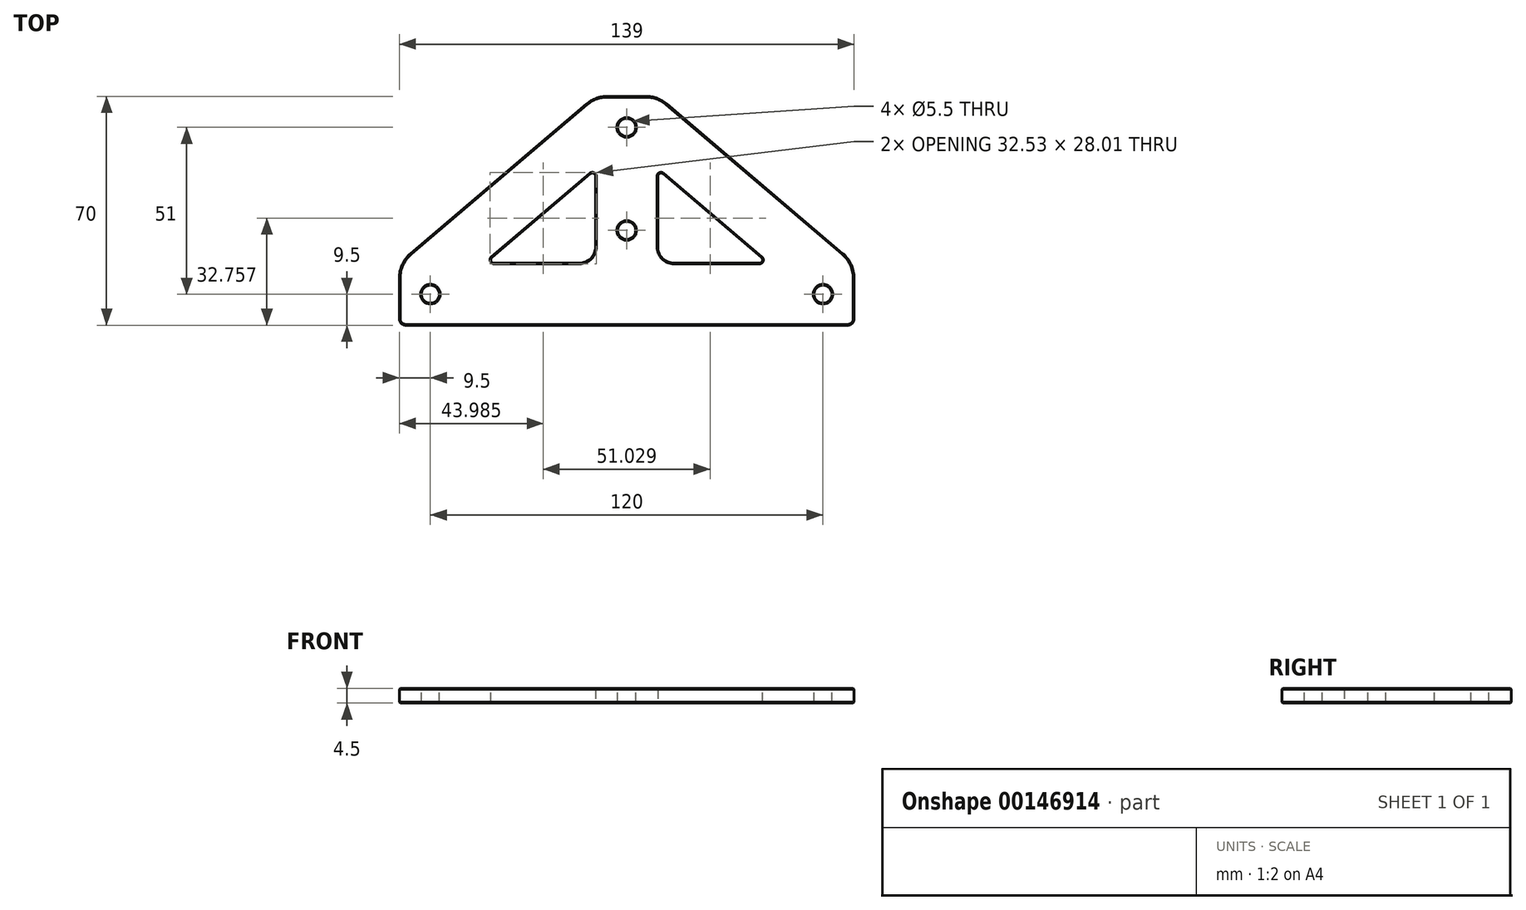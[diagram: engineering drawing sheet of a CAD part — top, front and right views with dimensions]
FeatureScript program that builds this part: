
annotation { "Feature Type Name" : "Feature", "Feature Type Description" : "" }
export const myFeature = defineFeature(function(context is Context, id is Id, definition is map)
    precondition{}
    {
        {
            var Q0;
            Q0=qCreatedBy(makeId("Top.planeOp"),FACE);
            var sketch = newSketch(context, id + "F0", { "sketchPlane" : qUnion([Q0])});
            skLineSegment(sketch, "E0", {"start": v(-69.5, 19) * mm, "end": v(-69.5, 0) * mm});
            skLineSegment(sketch, "E1", {"start": v(-69.5, 0) * mm, "end": v(69.5, 0) * mm});
            skLineSegment(sketch, "E2", {"start": v(69.5, 0) * mm, "end": v(69.5, 19) * mm});
            skLineSegment(sketch, "E3", {"start": v(69.5, 19) * mm, "end": v(9.5, 70) * mm});
            skLineSegment(sketch, "E4", {"start": v(9.5, 70) * mm, "end": v(-9.5, 70) * mm});
            skLineSegment(sketch, "E5", {"start": v(-9.5, 70) * mm, "end": v(-69.5, 19) * mm});
            skLineSegment(sketch, "E6", {"start": v(-9.5, 47.69) * mm, "end": v(-9.5, 19) * mm});
            skLineSegment(sketch, "E7", {"start": v(-9.5, 19) * mm, "end": v(-43.25, 19) * mm});
            skLineSegment(sketch, "E8", {"start": v(-43.25, 19) * mm, "end": v(-9.5, 47.69) * mm});
            skLineSegment(sketch, "E9.MirrorCS", {"start": v(9.5, 47.69) * mm, "end": v(9.5, 19) * mm});
            skLineSegment(sketch, "E10.MirrorCS", {"start": v(43.25, 19) * mm, "end": v(9.5, 47.69) * mm});
            skLineSegment(sketch, "E11.MirrorCS", {"start": v(9.5, 19) * mm, "end": v(43.25, 19) * mm});
            skSolve(sketch);
        }
        {
            var Q0;
            Q0 = qSketchRegion(id + "F0", true);
            extrude(context, id + "F1", {"entities" : qUnion([Q0]), "depth" : 4.5 * mm});
        }
        {
            var Q0;
            Q0=makeQuery(id+"F1.opExtrude","CAP_FACE",FACE,{"disambiguationData":[OSD([sQuery(id+"F0.wireOp",EDGE,"E0"),sQuery(id+"F0.wireOp",EDGE,"E1"),sQuery(id+"F0.wireOp",EDGE,"E2"),sQuery(id+"F0.wireOp",EDGE,"E3"),sQuery(id+"F0.wireOp",EDGE,"E4"),sQuery(id+"F0.wireOp",EDGE,"E5"),sQuery(id+"F0.wireOp",EDGE,"E6"),sQuery(id+"F0.wireOp",EDGE,"E7"),sQuery(id+"F0.wireOp",EDGE,"E8"),sQuery(id+"F0.wireOp",EDGE,"E9.MirrorCS"),sQuery(id+"F0.wireOp",EDGE,"E10.MirrorCS"),sQuery(id+"F0.wireOp",EDGE,"E11.MirrorCS")])],"isStart":false});
            var sketch = newSketch(context, id + "F2", { "sketchPlane" : qUnion([Q0])});
            skCircle(sketch, "E12", {"center": v(0, 60.5) * mm, "radius": 2.75 * mm});
            skCircle(sketch, "E13", {"center": v(0, 29) * mm, "radius": 2.75 * mm});
            skCircle(sketch, "E14", {"center": v(60, 9.5) * mm, "radius": 2.75 * mm});
            skCircle(sketch, "E15", {"center": v(-60, 9.5) * mm, "radius": 2.75 * mm});
            skSolve(sketch);
        }
        {
            var Q0;
            Q0 = qSketchRegion(id + "F2", true);
            extrude(context, id + "F3", {"entities" : qUnion([Q0]), "operationType" : NewBodyOperationType.REMOVE, "endBound" : BoundingType.THROUGH_ALL, "oppositeDirection" : true, "depth" : 25 * mm});
        }
        {
            var Q0;
            Q0=makeQuery(id+"F1.opExtrude","SWEPT_EDGE",EDGE,{"disambiguationData":[OSD([sQuery(id+"F0.wireOp",EDGE,"E6"),sQuery(id+"F0.wireOp",EDGE,"E7")])]});
            var Q1;
            Q1=makeQuery(id+"F1.opExtrude","SWEPT_EDGE",EDGE,{"disambiguationData":[OSD([sQuery(id+"F0.wireOp",EDGE,"E9.MirrorCS"),sQuery(id+"F0.wireOp",EDGE,"E11.MirrorCS")])]});
            fillet(context, id + "F4", {"entities" : qUnion([Q0, Q1]), "radius" : 5 * mm, "tangentPropagation" : true, "allowEdgeOverflow" : false});
        }
        {
            var Q0;
            Q0=makeQuery(id+"F1.opExtrude","SWEPT_EDGE",EDGE,{"disambiguationData":[OSD([sQuery(id+"F0.wireOp",EDGE,"E10.MirrorCS"),sQuery(id+"F0.wireOp",EDGE,"E11.MirrorCS")])]});
            var Q1;
            Q1=makeQuery(id+"F1.opExtrude","SWEPT_EDGE",EDGE,{"disambiguationData":[OSD([sQuery(id+"F0.wireOp",EDGE,"E9.MirrorCS"),sQuery(id+"F0.wireOp",EDGE,"E10.MirrorCS")])]});
            var Q2;
            Q2=makeQuery(id+"F1.opExtrude","SWEPT_EDGE",EDGE,{"disambiguationData":[OSD([sQuery(id+"F0.wireOp",EDGE,"E6"),sQuery(id+"F0.wireOp",EDGE,"E8")])]});
            var Q3;
            Q3=makeQuery(id+"F1.opExtrude","SWEPT_EDGE",EDGE,{"disambiguationData":[OSD([sQuery(id+"F0.wireOp",EDGE,"E7"),sQuery(id+"F0.wireOp",EDGE,"E8")])]});
            fillet(context, id + "F5", {"entities" : qUnion([Q0, Q1, Q2, Q3]), "radius" : 1 * mm, "tangentPropagation" : true, "allowEdgeOverflow" : false});
        }
        {
            var Q0;
            Q0=makeQuery(id+"F1.opExtrude","SWEPT_EDGE",EDGE,{"disambiguationData":[OSD([sQuery(id+"F0.wireOp",EDGE,"E4"),sQuery(id+"F0.wireOp",EDGE,"E5")])]});
            var Q1;
            Q1=makeQuery(id+"F1.opExtrude","SWEPT_EDGE",EDGE,{"disambiguationData":[OSD([sQuery(id+"F0.wireOp",EDGE,"E3"),sQuery(id+"F0.wireOp",EDGE,"E4")])]});
            var Q2;
            Q2=makeQuery(id+"F1.opExtrude","SWEPT_EDGE",EDGE,{"disambiguationData":[OSD([sQuery(id+"F0.wireOp",EDGE,"E0"),sQuery(id+"F0.wireOp",EDGE,"E5")])]});
            var Q3;
            Q3=makeQuery(id+"F1.opExtrude","SWEPT_EDGE",EDGE,{"disambiguationData":[OSD([sQuery(id+"F0.wireOp",EDGE,"E2"),sQuery(id+"F0.wireOp",EDGE,"E3")])]});
            fillet(context, id + "F6", {"entities" : qUnion([Q0, Q1, Q2, Q3]), "radius" : 10 * mm, "tangentPropagation" : true, "allowEdgeOverflow" : false});
        }
        {
            var Q0;
            Q0=makeQuery(id+"F1.opExtrude","SWEPT_EDGE",EDGE,{"disambiguationData":[OSD([sQuery(id+"F0.wireOp",EDGE,"E0"),sQuery(id+"F0.wireOp",EDGE,"E1")])]});
            var Q1;
            Q1=makeQuery(id+"F1.opExtrude","SWEPT_EDGE",EDGE,{"disambiguationData":[OSD([sQuery(id+"F0.wireOp",EDGE,"E1"),sQuery(id+"F0.wireOp",EDGE,"E2")])]});
            fillet(context, id + "F7", {"entities" : qUnion([Q0, Q1]), "radius" : 2 * mm, "tangentPropagation" : true, "allowEdgeOverflow" : false});
        }
        {
            var Q0;
            Q0=makeQuery(id+"F3.boolean.opBoolean","COPY",EDGE,{"derivedFrom":makeQuery(id+"F3.opExtrude","CAP_EDGE",EDGE,{"disambiguationData":[OSD([sQuery(id+"F2.wireOp",EDGE,"E12")])],"isStart":true})});
            var Q1;
            Q1=makeQuery(id+"F3.boolean.opBoolean","COPY",EDGE,{"derivedFrom":makeQuery(id+"F3.opExtrude","CAP_EDGE",EDGE,{"disambiguationData":[OSD([sQuery(id+"F2.wireOp",EDGE,"E13")])],"isStart":true})});
            var Q2;
            Q2=makeQuery(id+"F3.boolean.opBoolean","COPY",EDGE,{"derivedFrom":makeQuery(id+"F3.opExtrude","CAP_EDGE",EDGE,{"disambiguationData":[OSD([sQuery(id+"F2.wireOp",EDGE,"E14")])],"isStart":true})});
            var Q3;
            Q3=makeQuery(id+"F3.boolean.opBoolean","COPY",EDGE,{"derivedFrom":makeQuery(id+"F3.opExtrude","CAP_EDGE",EDGE,{"disambiguationData":[OSD([sQuery(id+"F2.wireOp",EDGE,"E15")])],"isStart":true})});
            var Q4;
            Q4=makeQuery(id+"F3.boolean.opBoolean","INTERSECT",EDGE,{"derivedFrom":[makeQuery(id+"F1.opExtrude","CAP_FACE",FACE,{"disambiguationData":[OSD([sQuery(id+"F0.wireOp",EDGE,"E0"),sQuery(id+"F0.wireOp",EDGE,"E1"),sQuery(id+"F0.wireOp",EDGE,"E2"),sQuery(id+"F0.wireOp",EDGE,"E3"),sQuery(id+"F0.wireOp",EDGE,"E4"),sQuery(id+"F0.wireOp",EDGE,"E5"),sQuery(id+"F0.wireOp",EDGE,"E6"),sQuery(id+"F0.wireOp",EDGE,"E7"),sQuery(id+"F0.wireOp",EDGE,"E8"),sQuery(id+"F0.wireOp",EDGE,"E9.MirrorCS"),sQuery(id+"F0.wireOp",EDGE,"E10.MirrorCS"),sQuery(id+"F0.wireOp",EDGE,"E11.MirrorCS")])],"isStart":true}),makeQuery(id+"F3.opExtrude","SWEPT_FACE",FACE,{"disambiguationData":[OSD([sQuery(id+"F2.wireOp",EDGE,"E12")])]})]});
            var Q5;
            Q5=makeQuery(id+"F3.boolean.opBoolean","INTERSECT",EDGE,{"derivedFrom":[makeQuery(id+"F1.opExtrude","CAP_FACE",FACE,{"disambiguationData":[OSD([sQuery(id+"F0.wireOp",EDGE,"E0"),sQuery(id+"F0.wireOp",EDGE,"E1"),sQuery(id+"F0.wireOp",EDGE,"E2"),sQuery(id+"F0.wireOp",EDGE,"E3"),sQuery(id+"F0.wireOp",EDGE,"E4"),sQuery(id+"F0.wireOp",EDGE,"E5"),sQuery(id+"F0.wireOp",EDGE,"E6"),sQuery(id+"F0.wireOp",EDGE,"E7"),sQuery(id+"F0.wireOp",EDGE,"E8"),sQuery(id+"F0.wireOp",EDGE,"E9.MirrorCS"),sQuery(id+"F0.wireOp",EDGE,"E10.MirrorCS"),sQuery(id+"F0.wireOp",EDGE,"E11.MirrorCS")])],"isStart":true}),makeQuery(id+"F3.opExtrude","SWEPT_FACE",FACE,{"disambiguationData":[OSD([sQuery(id+"F2.wireOp",EDGE,"E15")])]})]});
            var Q6;
            Q6=makeQuery(id+"F3.boolean.opBoolean","INTERSECT",EDGE,{"derivedFrom":[makeQuery(id+"F1.opExtrude","CAP_FACE",FACE,{"disambiguationData":[OSD([sQuery(id+"F0.wireOp",EDGE,"E0"),sQuery(id+"F0.wireOp",EDGE,"E1"),sQuery(id+"F0.wireOp",EDGE,"E2"),sQuery(id+"F0.wireOp",EDGE,"E3"),sQuery(id+"F0.wireOp",EDGE,"E4"),sQuery(id+"F0.wireOp",EDGE,"E5"),sQuery(id+"F0.wireOp",EDGE,"E6"),sQuery(id+"F0.wireOp",EDGE,"E7"),sQuery(id+"F0.wireOp",EDGE,"E8"),sQuery(id+"F0.wireOp",EDGE,"E9.MirrorCS"),sQuery(id+"F0.wireOp",EDGE,"E10.MirrorCS"),sQuery(id+"F0.wireOp",EDGE,"E11.MirrorCS")])],"isStart":true}),makeQuery(id+"F3.opExtrude","SWEPT_FACE",FACE,{"disambiguationData":[OSD([sQuery(id+"F2.wireOp",EDGE,"E13")])]})]});
            var Q7;
            Q7=makeQuery(id+"F3.boolean.opBoolean","INTERSECT",EDGE,{"derivedFrom":[makeQuery(id+"F1.opExtrude","CAP_FACE",FACE,{"disambiguationData":[OSD([sQuery(id+"F0.wireOp",EDGE,"E0"),sQuery(id+"F0.wireOp",EDGE,"E1"),sQuery(id+"F0.wireOp",EDGE,"E2"),sQuery(id+"F0.wireOp",EDGE,"E3"),sQuery(id+"F0.wireOp",EDGE,"E4"),sQuery(id+"F0.wireOp",EDGE,"E5"),sQuery(id+"F0.wireOp",EDGE,"E6"),sQuery(id+"F0.wireOp",EDGE,"E7"),sQuery(id+"F0.wireOp",EDGE,"E8"),sQuery(id+"F0.wireOp",EDGE,"E9.MirrorCS"),sQuery(id+"F0.wireOp",EDGE,"E10.MirrorCS"),sQuery(id+"F0.wireOp",EDGE,"E11.MirrorCS")])],"isStart":true}),makeQuery(id+"F3.opExtrude","SWEPT_FACE",FACE,{"disambiguationData":[OSD([sQuery(id+"F2.wireOp",EDGE,"E14")])]})]});
            var Q8;
            Q8=makeQuery(id+"F1.opExtrude","CAP_EDGE",EDGE,{"disambiguationData":[OSD([sQuery(id+"F0.wireOp",EDGE,"E1")])],"isStart":false});
            var Q9;
            Q9=makeQuery(id+"F1.opExtrude","CAP_EDGE",EDGE,{"disambiguationData":[OSD([sQuery(id+"F0.wireOp",EDGE,"E1")])],"isStart":true});
            var Q10;
            Q10=makeQuery(id+"F1.opExtrude","CAP_EDGE",EDGE,{"disambiguationData":[OSD([sQuery(id+"F0.wireOp",EDGE,"E7")])],"isStart":true});
            var Q11;
            Q11=makeQuery(id+"F1.opExtrude","CAP_FACE",FACE,{"disambiguationData":[OSD([sQuery(id+"F0.wireOp",EDGE,"E0"),sQuery(id+"F0.wireOp",EDGE,"E1"),sQuery(id+"F0.wireOp",EDGE,"E2"),sQuery(id+"F0.wireOp",EDGE,"E3"),sQuery(id+"F0.wireOp",EDGE,"E4"),sQuery(id+"F0.wireOp",EDGE,"E5"),sQuery(id+"F0.wireOp",EDGE,"E6"),sQuery(id+"F0.wireOp",EDGE,"E7"),sQuery(id+"F0.wireOp",EDGE,"E8"),sQuery(id+"F0.wireOp",EDGE,"E9.MirrorCS"),sQuery(id+"F0.wireOp",EDGE,"E10.MirrorCS"),sQuery(id+"F0.wireOp",EDGE,"E11.MirrorCS")])],"isStart":false});
            var Q12;
            Q12=makeQuery(id+"F1.opExtrude","CAP_FACE",FACE,{"disambiguationData":[OSD([sQuery(id+"F0.wireOp",EDGE,"E0"),sQuery(id+"F0.wireOp",EDGE,"E1"),sQuery(id+"F0.wireOp",EDGE,"E2"),sQuery(id+"F0.wireOp",EDGE,"E3"),sQuery(id+"F0.wireOp",EDGE,"E4"),sQuery(id+"F0.wireOp",EDGE,"E5"),sQuery(id+"F0.wireOp",EDGE,"E6"),sQuery(id+"F0.wireOp",EDGE,"E7"),sQuery(id+"F0.wireOp",EDGE,"E8"),sQuery(id+"F0.wireOp",EDGE,"E9.MirrorCS"),sQuery(id+"F0.wireOp",EDGE,"E10.MirrorCS"),sQuery(id+"F0.wireOp",EDGE,"E11.MirrorCS")])],"isStart":true});
            chamfer(context, id + "F8", {"entities" : qUnion([Q0, Q1, Q2, Q3, Q4, Q5, Q6, Q7, Q8, Q9, Q10, Q11, Q12]), "width" : .25 * mm, "tangentPropagation" : true});
        }
    });
